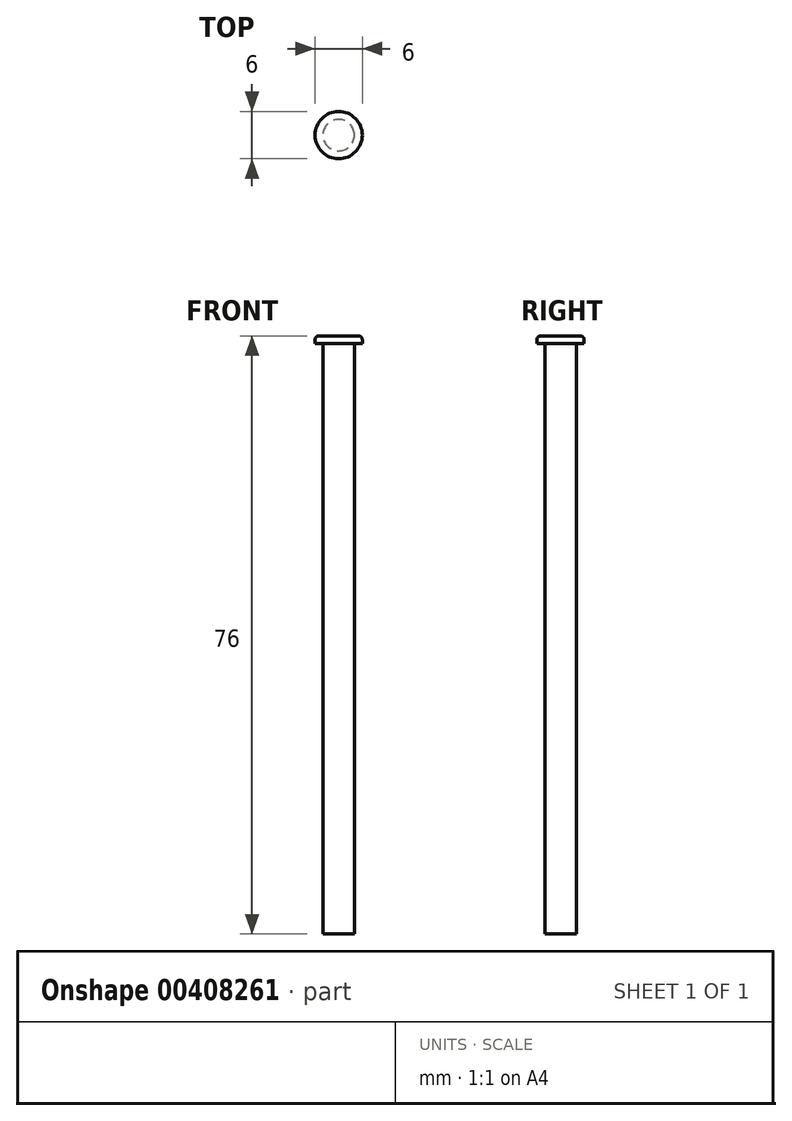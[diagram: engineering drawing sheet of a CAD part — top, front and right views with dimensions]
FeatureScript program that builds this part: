
annotation { "Feature Type Name" : "Feature", "Feature Type Description" : "" }
export const myFeature = defineFeature(function(context is Context, id is Id, definition is map)
    precondition{}
    {
        {
            var Q0;
            Q0=qCreatedBy(makeId("Top.planeOp"),FACE);
            var sketch = newSketch(context, id + "F0", { "sketchPlane" : qUnion([Q0])});
            skCircle(sketch, "E0", {"center": v(0, 0) * mm, "radius": 3 * mm});
            skSolve(sketch);
        }
        {
            var Q0;
            Q0 = qSketchRegion(id + "F0", true);
            extrude(context, id + "F1", {"entities" : qUnion([Q0]), "depth" : 1 * mm});
        }
        {
            var Q0;
            Q0=makeQuery(id+"F1.opExtrude","CAP_EDGE",EDGE,{"disambiguationData":[OSD([sQuery(id+"F0.wireOp",EDGE,"E0")])],"isStart":false});
            fillet(context, id + "F2", {"entities" : qUnion([Q0]), "radius" : .5 * mm, "tangentPropagation" : true, "allowEdgeOverflow" : false});
        }
        {
            var Q0;
            Q0=makeQuery(id+"F1.opExtrude","CAP_FACE",FACE,{"disambiguationData":[OSD([sQuery(id+"F0.wireOp",EDGE,"E0")])],"isStart":true});
            var sketch = newSketch(context, id + "F3", { "sketchPlane" : qUnion([Q0])});
            skCircle(sketch, "E1", {"center": v(0, 0) * mm, "radius": 2 * mm});
            skSolve(sketch);
        }
        {
            var Q0;
            Q0 = qSketchRegion(id + "F3", true);
            extrude(context, id + "F4", {"entities" : qUnion([Q0]), "operationType" : NewBodyOperationType.ADD, "depth" : 75 * mm});
        }
    });
